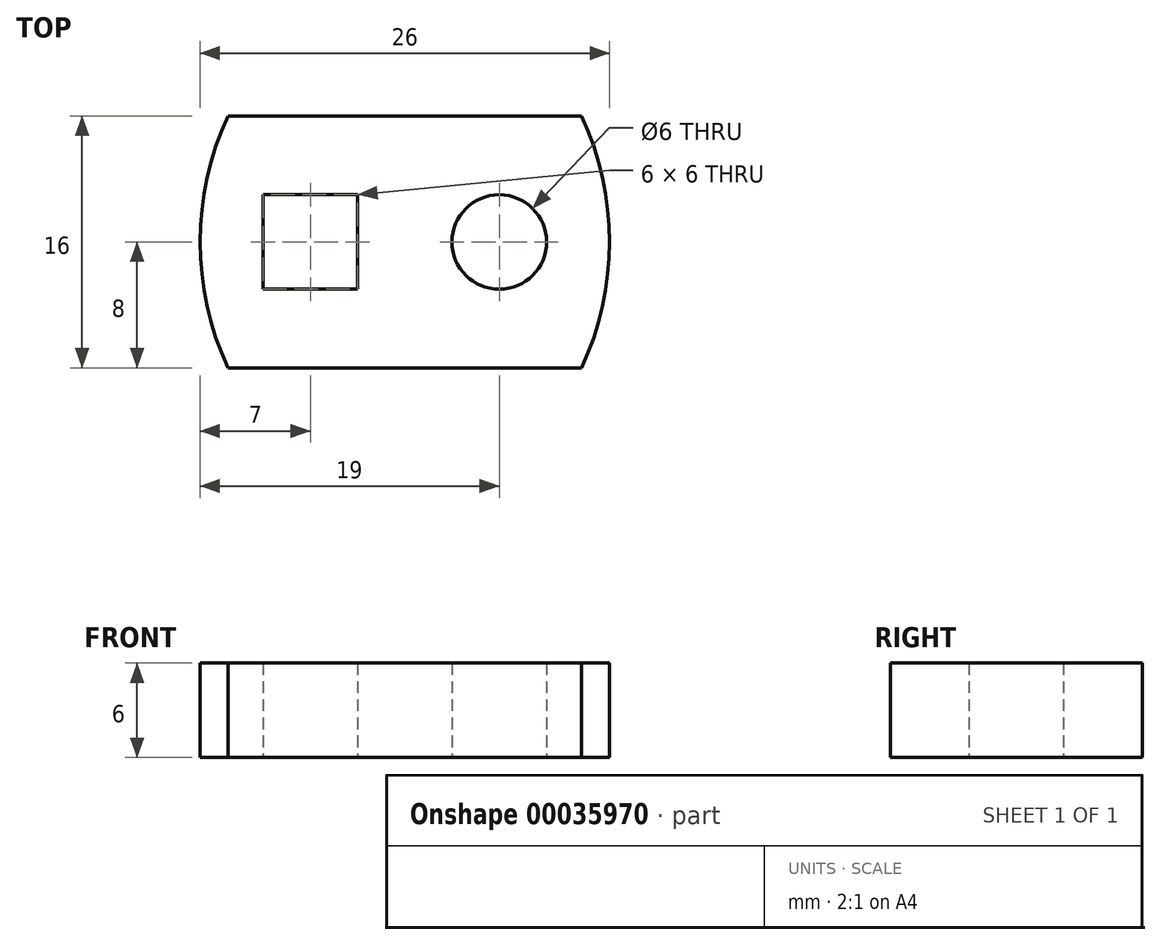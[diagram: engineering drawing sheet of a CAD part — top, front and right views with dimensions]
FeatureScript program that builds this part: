
annotation { "Feature Type Name" : "Feature", "Feature Type Description" : "" }
export const myFeature = defineFeature(function(context is Context, id is Id, definition is map)
    precondition{}
    {
        {
            var Q0;
            Q0=qCreatedBy(makeId("Top.planeOp"),FACE);
            var sketch = newSketch(context, id + "F0", { "sketchPlane" : qUnion([Q0])});
            skCircle(sketch, "E0", {"center": v(0, 0) * mm, "radius": 3 * mm});
            skLineSegment(sketch, "E1", {"start": v(0, 0) * mm, "end": v(-12, 0) * mm});
            skLineSegment(sketch, "E2.bottom", {"start": v(-9, -3) * mm, "end": v(-15, -3) * mm});
            skLineSegment(sketch, "E2.top", {"start": v(-9, 3) * mm, "end": v(-15, 3) * mm});
            skLineSegment(sketch, "E2.left", {"start": v(-9, -3) * mm, "end": v(-9, 3) * mm});
            skLineSegment(sketch, "E2.right", {"start": v(-15, -3) * mm, "end": v(-15, 3) * mm});
            skPoint(sketch, "E2.middle", {"position": v(-12, 0) * mm});
            skArc(sketch, "E3", {"start": v(-17.23, 8) * mm, "mid": v(-19, 0) * mm, "end": v(-17.23, -8) * mm});
            skLineSegment(sketch, "E4", {"start": v(0, 0) * mm, "end": v(0, 8) * mm});
            skLineSegment(sketch, "E5", {"start": v(0, 8) * mm, "end": v(-17.23, 8) * mm});
            skLineSegment(sketch, "E6", {"start": v(-17.23, -8) * mm, "end": v(5.23, -8) * mm});
            skArc(sketch, "E7.trimOffspring", {"start": v(5.23, -8) * mm, "mid": v(7, 0) * mm, "end": v(5.23, 8) * mm});
            skLineSegment(sketch, "E8.trimOffspring", {"start": v(5.23, 8) * mm, "end": v(0, 8) * mm});
            skPoint(sketch, "E9.end.orphan", {"position": v(43, 8) * mm});
            skSolve(sketch);
        }
        {
            var Q0;
            {var subQ6=sQuery(id+"F0.wireOp",EDGE,"E2.bottom");Q0=makeQuery(id+"F0.imprint","IMPRINT",FACE,{"disambiguationData":[TD([[makeQuery(id+"F0.imprint","IMPRINT",EDGE,{"derivedFrom":subQ6}),1.0]])]});}
            extrude(context, id + "F1", {"entities" : qUnion([Q0]), "depth" : 6 * mm});
        }
    });
